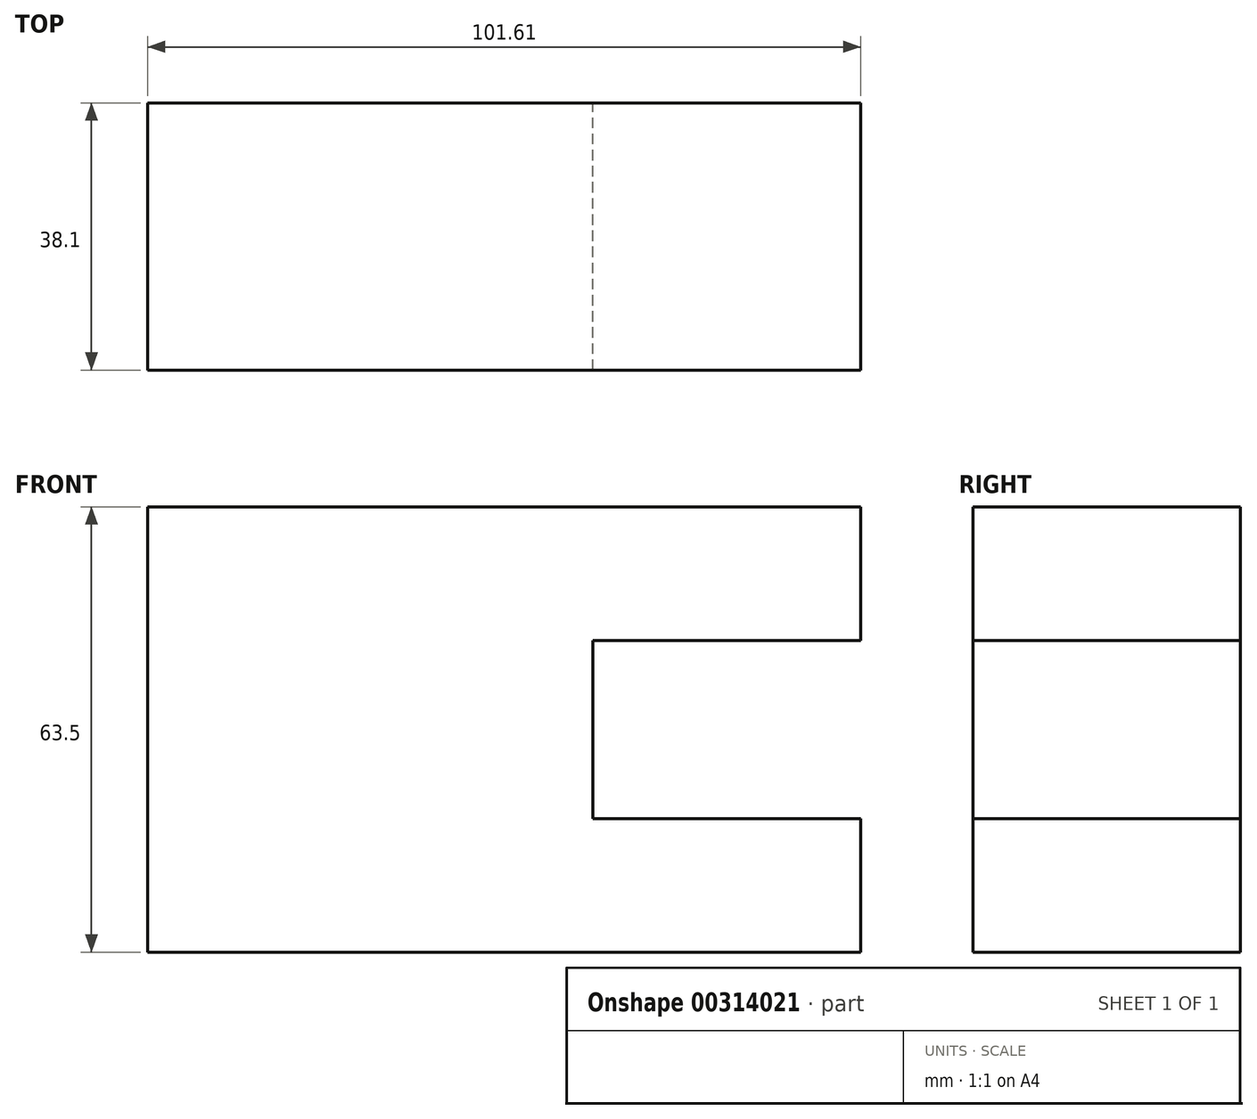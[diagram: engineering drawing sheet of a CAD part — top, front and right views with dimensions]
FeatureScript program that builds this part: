
annotation { "Feature Type Name" : "Feature", "Feature Type Description" : "" }
export const myFeature = defineFeature(function(context is Context, id is Id, definition is map)
    precondition{}
    {
        {
            var Q0;
            Q0=qCreatedBy(makeId("Front.planeOp"),FACE);
            var sketch = newSketch(context, id + "F0", { "sketchPlane" : qUnion([Q0])});
            skLineSegment(sketch, "E0", {"start": v(-51.55, 35.46) * mm, "end": v(-51.55, -28.04) * mm});
            skLineSegment(sketch, "E1", {"start": v(-51.55, 35.46) * mm, "end": v(50.06, 35.46) * mm});
            skLineSegment(sketch, "E2", {"start": v(-51.55, -28.04) * mm, "end": v(50.06, -28.04) * mm});
            skLineSegment(sketch, "E3", {"start": v(50.06, 35.46) * mm, "end": v(50.06, 16.4) * mm});
            skLineSegment(sketch, "E4", {"start": v(50.06, -28.04) * mm, "end": v(50.06, -9) * mm});
            skLineSegment(sketch, "E5", {"start": v(50.06, -9) * mm, "end": v(11.87, -9) * mm});
            skLineSegment(sketch, "E6", {"start": v(50.06, 16.4) * mm, "end": v(11.87, 16.4) * mm});
            skLineSegment(sketch, "E7", {"start": v(11.87, 16.4) * mm, "end": v(11.87, -9) * mm});
            skSolve(sketch);
        }
        {
            var Q0;
            Q0 = qSketchRegion(id + "F0", true);
            extrude(context, id + "F1", {"entities" : qUnion([Q0]), "depth" : 38.1 * mm});
        }
    });
